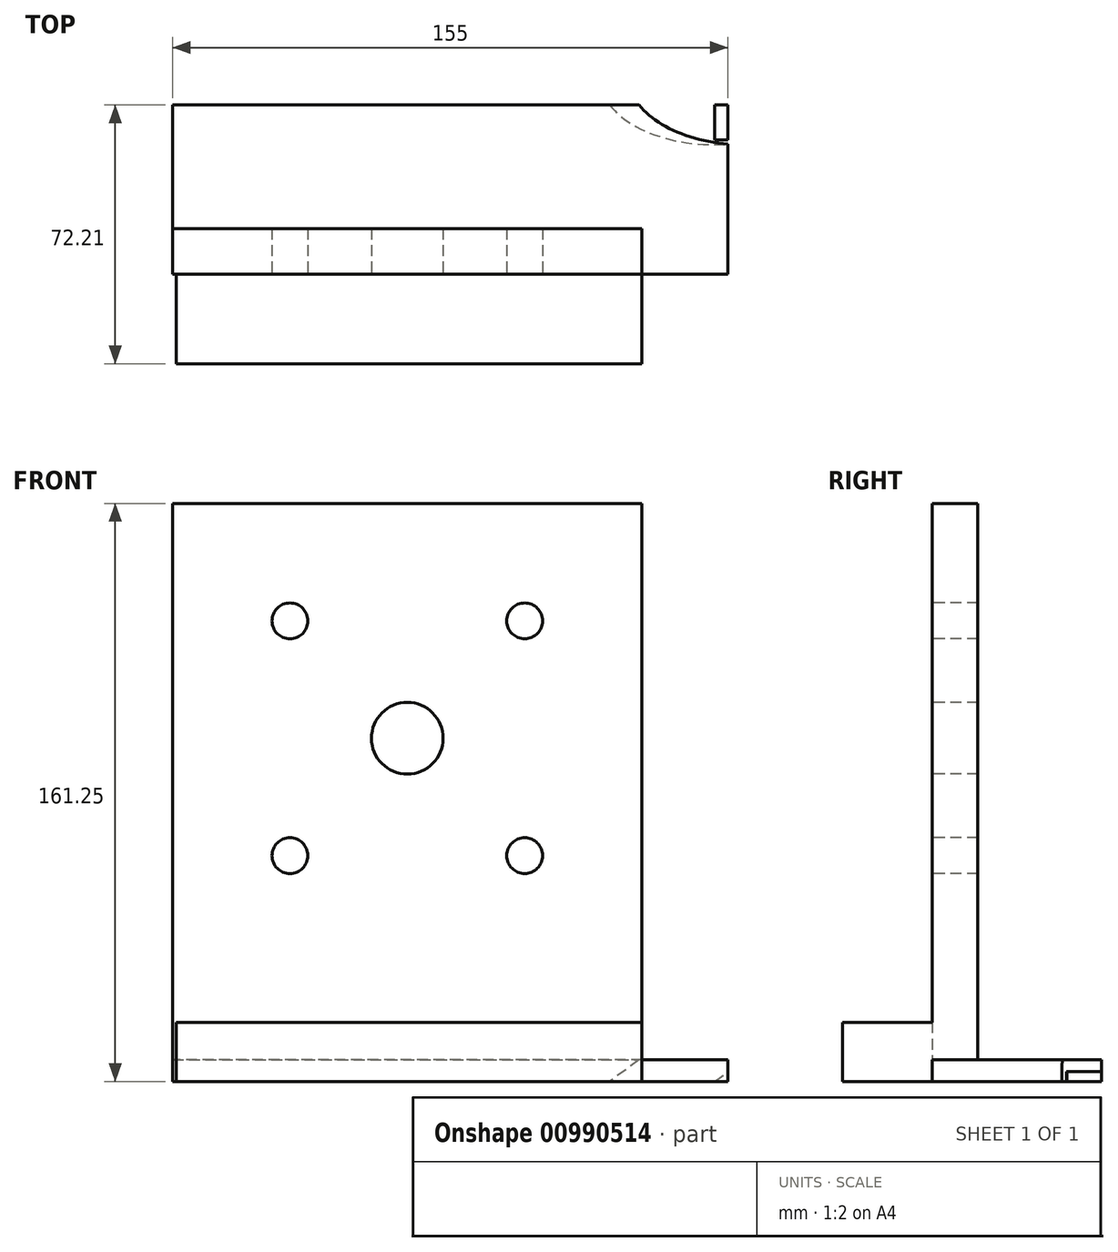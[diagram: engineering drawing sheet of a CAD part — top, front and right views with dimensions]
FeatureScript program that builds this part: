
annotation { "Feature Type Name" : "Feature", "Feature Type Description" : "" }
export const myFeature = defineFeature(function(context is Context, id is Id, definition is map)
    precondition{}
    {
        {
            var Q0;
            Q0=qCreatedBy(makeId("Front.planeOp"),FACE);
            var sketch = newSketch(context, id + "F0", { "sketchPlane" : qUnion([Q0])});
            skLineSegment(sketch, "E0.bottom", {"start": v(65.5, 0) * mm, "end": v(-65.5, 0) * mm});
            skLineSegment(sketch, "E0.top", {"start": v(65.5, 155.25) * mm, "end": v(-65.5, 155.25) * mm});
            skLineSegment(sketch, "E0.left", {"start": v(65.5, 0) * mm, "end": v(65.5, 155.25) * mm});
            skLineSegment(sketch, "E0.right", {"start": v(-65.5, 0) * mm, "end": v(-65.5, 155.25) * mm});
            skLineSegment(sketch, "E1.bottom", {"start": v(-65.5, 0) * mm, "end": v(89.5, 0) * mm});
            skLineSegment(sketch, "E1.top", {"start": v(-65.5, -12.7) * mm, "end": v(89.5, -12.7) * mm});
            skLineSegment(sketch, "E1.left", {"start": v(-65.5, 0) * mm, "end": v(-65.5, -12.7) * mm});
            skLineSegment(sketch, "E1.right", {"start": v(89.5, 0) * mm, "end": v(89.5, -12.7) * mm});
            skCircle(sketch, "E2", {"center": v(-32.75, 57) * mm, "radius": 5 * mm});
            skCircle(sketch, "E3.0.1.0", {"center": v(-32.75, 122.5) * mm, "radius": 5 * mm});
            skCircle(sketch, "E3.1.0.0", {"center": v(32.75, 57) * mm, "radius": 5 * mm});
            skCircle(sketch, "E3.1.1.0", {"center": v(32.75, 122.5) * mm, "radius": 5 * mm});
            skLineSegment(sketch, "E3.direction1", {"start": v(-32.75, 57) * mm, "end": v(32.75, 57) * mm, "construction": true});
            skLineSegment(sketch, "E3.direction2", {"start": v(-32.75, 57) * mm, "end": v(-32.75, 122.5) * mm, "construction": true});
            skCircle(sketch, "E4", {"center": v(0, 89.75) * mm, "radius": 10 * mm});
            skSolve(sketch);
        }
        {
            var Q0;
            Q0=makeQuery(id+"F0.imprint","IMPRINT",FACE,{"disambiguationData":[TD([[makeQuery(id+"F0.imprint","IMPRINT",EDGE,{"derivedFrom":sQuery(id+"F0.wireOp",EDGE,"E0.top")}),1.0]])]});
            extrude(context, id + "F1", {"entities" : qUnion([Q0]), "oppositeDirection" : true, "depth" : 12.7 * mm, "offsetDistance" : 25 * mm});
        }
        {
            var Q0;
            Q0=makeQuery(id+"F0.imprint","IMPRINT",FACE,{"disambiguationData":[TD([[makeQuery(id+"F0.imprint","IMPRINT",EDGE,{"derivedFrom":sQuery(id+"F0.wireOp",EDGE,"E1.bottom")}),-1.0]])]});
            extrude(context, id + "F2", {"entities" : qUnion([Q0]), "operationType" : NewBodyOperationType.ADD, "oppositeDirection" : true, "depth" : 150 * mm, "offsetDistance" : 25 * mm});
        }
        {
            var Q0;
            Q0=makeQuery(id+"F2.opExtrude","SWEPT_FACE",FACE,{"disambiguationData":[OSD([sQuery(id+"F0.wireOp",EDGE,"E1.top")])]});
            var sketch = newSketch(context, id + "F3", { "sketchPlane" : qUnion([Q0])});
            skLineSegment(sketch, "E5", {"start": v(89.5, -12.7) * mm, "end": v(-65.5, -12.7) * mm});
            skCircle(sketch, "E6", {"center": v(-40, -55.7) * mm, "radius": 4.76 * mm});
            skCircle(sketch, "E7.0.1.0", {"center": v(-40, -118.2) * mm, "radius": 4.76 * mm});
            skCircle(sketch, "E7.1.0.0", {"center": v(64, -55.7) * mm, "radius": 4.76 * mm});
            skCircle(sketch, "E7.1.1.0", {"center": v(64, -118.2) * mm, "radius": 4.76 * mm});
            skLineSegment(sketch, "E7.direction1", {"start": v(-40, -55.7) * mm, "end": v(64, -55.7) * mm, "construction": true});
            skLineSegment(sketch, "E7.direction2", {"start": v(-40, -55.7) * mm, "end": v(-40, -118.2) * mm, "construction": true});
            skSolve(sketch);
        }
        {
            var Q0;
            Q0=makeQuery(id+"F3.imprint","IMPRINT",FACE,{"disambiguationData":[TD([[makeQuery(id+"F3.imprint","IMPRINT",EDGE,{"derivedFrom":sQuery(id+"F3.wireOp",EDGE,"E6")}),1.0]])]});
            var Q1;
            Q1=makeQuery(id+"F3.imprint","IMPRINT",FACE,{"disambiguationData":[TD([[makeQuery(id+"F3.imprint","IMPRINT",EDGE,{"derivedFrom":sQuery(id+"F3.wireOp",EDGE,"E7.0.1.0")}),1.0]])]});
            var Q2;
            Q2=makeQuery(id+"F3.imprint","IMPRINT",FACE,{"disambiguationData":[TD([[makeQuery(id+"F3.imprint","IMPRINT",EDGE,{"derivedFrom":sQuery(id+"F3.wireOp",EDGE,"E7.1.1.0")}),1.0]])]});
            var Q3;
            Q3=makeQuery(id+"F3.imprint","IMPRINT",FACE,{"disambiguationData":[TD([[makeQuery(id+"F3.imprint","IMPRINT",EDGE,{"derivedFrom":sQuery(id+"F3.wireOp",EDGE,"E7.1.0.0")}),1.0]])]});
            extrude(context, id + "F4", {"entities" : qUnion([Q0, Q1, Q2, Q3]), "operationType" : NewBodyOperationType.REMOVE, "endBound" : BoundingType.THROUGH_ALL, "oppositeDirection" : true, "depth" : 25 * mm, "offsetDistance" : 25 * mm});
        }
        {
            var Q0;
            {var subQ0=sQuery(id+"F0.wireOp",EDGE,"E1.bottom");Q0=makeQuery(id+"F2.boolean.opBoolean","MERGE",FACE,{"derivedFrom":[makeQuery(id+"F1.opExtrude","CAP_FACE",FACE,{"disambiguationData":[OSD([sQuery(id+"F0.wireOp",EDGE,"E0.top"),sQuery(id+"F0.wireOp",EDGE,"E0.left"),sQuery(id+"F0.wireOp",EDGE,"E0.right"),subQ0,sQuery(id+"F0.wireOp",EDGE,"E2"),sQuery(id+"F0.wireOp",EDGE,"E3.0.1.0"),sQuery(id+"F0.wireOp",EDGE,"E3.1.0.0"),sQuery(id+"F0.wireOp",EDGE,"E3.1.1.0"),sQuery(id+"F0.wireOp",EDGE,"E4")])],"isStart":true}),makeQuery(id+"F2.opExtrude","CAP_FACE",FACE,{"disambiguationData":[OSD([subQ0,sQuery(id+"F0.wireOp",EDGE,"E1.top"),sQuery(id+"F0.wireOp",EDGE,"E1.left"),sQuery(id+"F0.wireOp",EDGE,"E1.right")])],"isStart":true})]});}
            var sketch = newSketch(context, id + "F5", { "sketchPlane" : qUnion([Q0])});
            skLineSegment(sketch, "E8", {"start": v(-63.5, -12.7) * mm, "end": v(-44.93, -100.76) * mm});
            skLineSegment(sketch, "E9", {"start": v(-44.93, -100.76) * mm, "end": v(76.5, -12.7) * mm});
            skSolve(sketch);
        }
        {
            var Q0;
            {var subQ0=sQuery(id+"F5.wireOp",EDGE,"E8");Q0=makeQuery(id+"F5.imprint","IMPRINT",FACE,{"disambiguationData":[TD([[makeQuery(id+"F5.imprint","IMPRINT",EDGE,{"derivedFrom":subQ0}),1.0]])]});}
            extrude(context, id + "F6", {"entities" : qUnion([Q0]), "operationType" : NewBodyOperationType.ADD, "oppositeDirection" : true, "depth" : 55 * mm, "offsetDistance" : 25 * mm});
        }
        {
            var Q0;
            Q0=makeQuery(id+"F6.opExtrude","SWEPT_FACE",FACE,{"disambiguationData":[OSD([sQuery(id+"F5.wireOp",EDGE,"E9")])]});
            var sketch = newSketch(context, id + "F7", { "sketchPlane" : qUnion([Q0])});
            skLineSegment(sketch, "E10", {"start": v(54.47, -55) * mm, "end": v(-45.53, -55) * mm});
            skLineSegment(sketch, "E11", {"start": v(-45.53, -55) * mm, "end": v(-45.53, -30) * mm});
            skLineSegment(sketch, "E12", {"start": v(-45.53, -30) * mm, "end": v(54.47, -30) * mm});
            skLineSegment(sketch, "E13", {"start": v(54.47, -30) * mm, "end": v(54.47, -55) * mm});
            skLineSegment(sketch, "E14", {"start": v(-45.53, -37.5) * mm, "end": v(18.27, -37.5) * mm});
            skLineSegment(sketch, "E15", {"start": v(18.27, -37.5) * mm, "end": v(54.47, -37.5) * mm});
            skSolve(sketch);
        }
        {
            var Q0;
            {var subQ2=sQuery(id+"F7.wireOp",EDGE,"E12");Q0=makeQuery(id+"F7.imprint","IMPRINT",FACE,{"disambiguationData":[TD([[makeQuery(id+"F7.imprint","IMPRINT",EDGE,{"derivedFrom":subQ2}),-1.0]])]});}
            var Q1;
            Q1=sQuery(id+"F7.wireOp",EDGE,"E10");
            revolve(context, id + "F8", {"operationType" : NewBodyOperationType.ADD, "surfaceOperationType" : NewSurfaceOperationType.NEW, "entities" : qUnion([Q0]), "axis" : qUnion([Q1]), "revolveType" : RevolveType.FULL, "oppositeDirection" : true});
        }
        {
            var Q0;
            Q0=makeQuery(id+"F2.opExtrude","SWEPT_FACE",FACE,{"disambiguationData":[OSD([sQuery(id+"F0.wireOp",EDGE,"E1.right")])]});
            var sketch = newSketch(context, id + "F9", { "sketchPlane" : qUnion([Q0])});
            skLineSegment(sketch, "E16.bottom", {"start": v(34.14, 0) * mm, "end": v(80.6, 0) * mm});
            skLineSegment(sketch, "E16.top", {"start": v(34.14, 23.6) * mm, "end": v(80.6, 23.6) * mm});
            skLineSegment(sketch, "E16.left", {"start": v(34.14, 0) * mm, "end": v(34.14, 23.6) * mm});
            skLineSegment(sketch, "E16.right", {"start": v(80.6, 0) * mm, "end": v(80.6, 23.6) * mm});
            skSolve(sketch);
        }
        {
            var Q0;
            Q0=makeQuery(id+"F9.imprint","IMPRINT",FACE,{"disambiguationData":[TD([[makeQuery(id+"F9.imprint","IMPRINT",EDGE,{"derivedFrom":sQuery(id+"F9.wireOp",EDGE,"E16.bottom")}),-1.0]])]});
            extrude(context, id + "F10", {"entities" : qUnion([Q0]), "operationType" : NewBodyOperationType.REMOVE, "oppositeDirection" : true, "depth" : 100.62 * mm, "offsetDistance" : 25 * mm});
        }
        {
            var Q0;
            Q0=qCreatedBy(makeId("Front.planeOp"),FACE);
            var sketch = newSketch(context, id + "F11", { "sketchPlane" : qUnion([Q0])});
            skLineSegment(sketch, "E17.bottom", {"start": v(-4.59, -72.84) * mm, "end": v(-55.62, -72.84) * mm});
            skLineSegment(sketch, "E17.top", {"start": v(-4.59, -104.11) * mm, "end": v(-55.62, -104.11) * mm});
            skLineSegment(sketch, "E17.left", {"start": v(-4.59, -72.84) * mm, "end": v(-4.59, -104.11) * mm});
            skLineSegment(sketch, "E17.right", {"start": v(-55.62, -72.84) * mm, "end": v(-55.62, -104.11) * mm});
            skLineSegment(sketch, "E18.bottom", {"start": v(-63.9, -12.7) * mm, "end": v(-44.63, -12.7) * mm});
            skLineSegment(sketch, "E18.top", {"start": v(-63.9, -72.84) * mm, "end": v(-44.63, -72.84) * mm});
            skLineSegment(sketch, "E18.left", {"start": v(-63.9, -12.7) * mm, "end": v(-63.9, -72.84) * mm});
            skLineSegment(sketch, "E18.right", {"start": v(-44.63, -12.7) * mm, "end": v(-44.63, -72.84) * mm});
            skSolve(sketch);
        }
        {
            var Q0;
            Q0=makeQuery(id+"F11.imprint","IMPRINT",FACE,{"disambiguationData":[TD([[makeQuery(id+"F11.imprint","IMPRINT",EDGE,{"derivedFrom":sQuery(id+"F11.wireOp",EDGE,"E18.bottom")}),-1.0]])]});
            var Q1;
            {var subQ1=sQuery(id+"F11.wireOp",EDGE,"E17.bottom");Q1=makeQuery(id+"F11.imprint","IMPRINT",FACE,{"disambiguationData":[TD([[makeQuery(id+"F11.imprint","IMPRINT",EDGE,{"derivedFrom":subQ1}),1.0]])]});}
            extrude(context, id + "F12", {"entities" : qUnion([Q0, Q1]), "operationType" : NewBodyOperationType.REMOVE, "endBound" : BoundingType.THROUGH_ALL, "oppositeDirection" : true, "depth" : 63.06 * mm, "offsetDistance" : 25 * mm});
        }
        {
            var Q0;
            Q0=makeQuery(id+"F6.opExtrude","CAP_FACE",FACE,{"disambiguationData":[OSD([sQuery(id+"F0.wireOp",EDGE,"E1.top"),sQuery(id+"F5.wireOp",EDGE,"E8"),sQuery(id+"F5.wireOp",EDGE,"E9")])],"isStart":false});
            var sketch = newSketch(context, id + "F13", { "sketchPlane" : qUnion([Q0])});
            skLineSegment(sketch, "E19", {"start": v(19.13, -51.17) * mm, "end": v(-10.05, -91.4) * mm});
            skLineSegment(sketch, "E20", {"start": v(-10.05, -91.4) * mm, "end": v(37.2, -125.68) * mm});
            skLineSegment(sketch, "E21", {"start": v(37.2, -125.68) * mm, "end": v(76.4, -71.65) * mm});
            skLineSegment(sketch, "E22", {"start": v(76.4, -71.65) * mm, "end": v(19.13, -51.17) * mm});
            skSolve(sketch);
        }
        {
            var Q0;
            {var subQ10=sQuery(id+"F13.wireOp",EDGE,"E20");Q0=makeQuery(id+"F13.imprint","IMPRINT",FACE,{"disambiguationData":[TD([[makeQuery(id+"F13.imprint","IMPRINT",EDGE,{"derivedFrom":subQ10}),1.0]])]});}
            var Q1;
            {var subQ0=sQuery(id+"F5.wireOp",EDGE,"E9");var subQ1=makeQuery(id+"F6.opExtrude","CAP_FACE",FACE,{"disambiguationData":[OSD([sQuery(id+"F0.wireOp",EDGE,"E1.top"),sQuery(id+"F5.wireOp",EDGE,"E8"),subQ0])],"isStart":false});var subQ2=subQ1;var subQ3=makeQuery(id+"F12.boolean.opBoolean","INTERSECT",EDGE,{"derivedFrom":[subQ2,makeQuery(id+"F12.opExtrude","SWEPT_FACE",FACE,{"disambiguationData":[OSD([sQuery(id+"F11.wireOp",EDGE,"E17.bottom")])]})]});Q1=makeQuery(id+"F13.imprint","IMPRINT",FACE,{"disambiguationData":[TD([[makeQuery(id+"F13.imprint","IMPRINT",EDGE,{"derivedFrom":subQ3}),1.0]])]});}
            extrude(context, id + "F14", {"entities" : qUnion([Q0, Q1]), "operationType" : NewBodyOperationType.REMOVE, "oppositeDirection" : true, "depth" : 89 * mm, "offsetDistance" : 25 * mm});
        }
        {
            var Q0;
            Q0=makeQuery(id+"F14.boolean.opBoolean","MERGE",FACE,{"derivedFrom":[makeQuery(id+"F8.opRevolve","SWEPT_FACE",FACE,{"disambiguationData":[OSD([sQuery(id+"F7.wireOp",EDGE,"E11")])]})],"fromTools":[makeQuery(id+"F14.opExtrude","SWEPT_FACE",FACE,{"disambiguationData":[OSD([sQuery(id+"F13.wireOp",EDGE,"E19")])]})]});
            var sketch = newSketch(context, id + "F15", { "sketchPlane" : qUnion([Q0])});
            skCircle(sketch, "E23", {"center": v(-55, -55.2) * mm, "radius": 18.87 * mm});
            skSolve(sketch);
        }
        {
            var Q0;
            {var subQ0=sQuery(id+"F13.wireOp",EDGE,"E19");Q0=makeQuery(id+"F15.imprint","IMPRINT",FACE,{"disambiguationData":[TD([[makeQuery(id+"F15.imprint","IMPRINT",EDGE,{"derivedFrom":makeQuery(id+"F14.boolean.opBoolean","COPY",EDGE,{"derivedFrom":makeQuery(id+"F14.opExtrude","CAP_EDGE",EDGE,{"disambiguationData":[OSD([subQ0])],"isStart":true})})}),-1.0]])]});}
            var Q1;
            Q1=makeQuery(id+"F15.imprint","IMPRINT",FACE,{"disambiguationData":[TD([[makeQuery(id+"F15.imprint","IMPRINT",EDGE,{"derivedFrom":sQuery(id+"F15.wireOp",EDGE,"E23")}),1.0]])]});
            extrude(context, id + "F16", {"entities" : qUnion([Q0, Q1]), "operationType" : NewBodyOperationType.REMOVE, "endBound" : BoundingType.THROUGH_ALL, "oppositeDirection" : true, "depth" : 25 * mm, "offsetDistance" : 25 * mm});
        }
        {
            var Q0;
            {var subQ1=sQuery(id+"F0.wireOp",EDGE,"E1.right");var subQ3=sQuery(id+"F0.wireOp",EDGE,"E1.top");var subQ6=makeQuery(id+"F2.opExtrude","SWEPT_FACE",FACE,{"disambiguationData":[OSD([subQ3])]});var subQ14=makeQuery(id+"F2.opExtrude","SWEPT_FACE",FACE,{"disambiguationData":[OSD([subQ1])]});var subQ17=makeQuery(id+"F4.boolean.opBoolean","COPY",FACE,{"derivedFrom":makeQuery(id+"F4.opExtrude","SWEPT_FACE",FACE,{"disambiguationData":[OSD([sQuery(id+"F3.wireOp",EDGE,"E6")])]})});Q0=makeQuery(id+"F16.boolean.opBoolean","SPLIT",FACE,{"disambiguationData":[TD([subQ17])],"derivedFrom":makeQuery(id+"F12.boolean.opBoolean","SPLIT",FACE,{"disambiguationData":[TD([subQ14])],"derivedFrom":subQ6})});}
            cPlane(context, id + "F17", {"entities" : qUnion([Q0]), "cplaneType" : CPlaneType.OFFSET, "offset" : 57.01 * mm, "width" : 150 * mm, "height" : 150 * mm});
        }
        {
            var Q0;
            Q0=qCreatedBy(id+"F17.planeOp",FACE);
            var sketch = newSketch(context, id + "F18", { "sketchPlane" : qUnion([Q0])});
            skLineSegment(sketch, "E24.bottom", {"start": v(-26.24, -39.17) * mm, "end": v(-54.25, -39.17) * mm});
            skLineSegment(sketch, "E24.top", {"start": v(-26.24, -72.55) * mm, "end": v(-54.25, -72.55) * mm});
            skLineSegment(sketch, "E24.left", {"start": v(-26.24, -39.17) * mm, "end": v(-26.24, -72.55) * mm});
            skLineSegment(sketch, "E24.right", {"start": v(-54.25, -39.17) * mm, "end": v(-54.25, -72.55) * mm});
            skSolve(sketch);
        }
        {
            var Q0;
            Q0=makeQuery(id+"F18.imprint","IMPRINT",FACE,{"disambiguationData":[TD([[makeQuery(id+"F18.imprint","IMPRINT",EDGE,{"derivedFrom":sQuery(id+"F18.wireOp",EDGE,"E24.bottom")}),1.0]])]});
            extrude(context, id + "F19", {"entities" : qUnion([Q0]), "operationType" : NewBodyOperationType.REMOVE, "oppositeDirection" : true, "depth" : 57.44 * mm, "offsetDistance" : 25 * mm});
        }
        {
            var Q0;
            {var subQ1=sQuery(id+"F0.wireOp",EDGE,"E1.right");var subQ3=sQuery(id+"F0.wireOp",EDGE,"E1.top");var subQ6=makeQuery(id+"F2.opExtrude","SWEPT_FACE",FACE,{"disambiguationData":[OSD([subQ3])]});var subQ14=makeQuery(id+"F2.opExtrude","SWEPT_FACE",FACE,{"disambiguationData":[OSD([subQ1])]});var subQ17=makeQuery(id+"F4.boolean.opBoolean","COPY",FACE,{"derivedFrom":makeQuery(id+"F4.opExtrude","SWEPT_FACE",FACE,{"disambiguationData":[OSD([sQuery(id+"F3.wireOp",EDGE,"E6")])]})});Q0=makeQuery(id+"F16.boolean.opBoolean","SPLIT",FACE,{"disambiguationData":[TD([subQ17])],"derivedFrom":makeQuery(id+"F12.boolean.opBoolean","SPLIT",FACE,{"disambiguationData":[TD([subQ14])],"derivedFrom":subQ6})});}
            cPlane(context, id + "F20", {"entities" : qUnion([Q0]), "cplaneType" : CPlaneType.OFFSET, "offset" : 94.9 * mm, "width" : 150 * mm, "height" : 150 * mm});
        }
        {
            var Q0;
            Q0=makeQuery(id+"F2.opExtrude","CAP_FACE",FACE,{"disambiguationData":[OSD([sQuery(id+"F0.wireOp",EDGE,"E1.bottom"),sQuery(id+"F0.wireOp",EDGE,"E1.top"),sQuery(id+"F0.wireOp",EDGE,"E1.left"),sQuery(id+"F0.wireOp",EDGE,"E1.right")])],"isStart":false});
            cPlane(context, id + "F21", {"entities" : qUnion([Q0]), "cplaneType" : CPlaneType.OFFSET, "offset" : 83.64 * mm, "oppositeDirection" : true, "width" : 150 * mm, "height" : 150 * mm});
        }
        {
            var Q0;
            Q0=qCreatedBy(id+"F21.planeOp",FACE);
            var sketch = newSketch(context, id + "F22", { "sketchPlane" : qUnion([Q0])});
            skLineSegment(sketch, "E25.bottom", {"start": v(-19.5, -47.14) * mm, "end": v(25.5, -47.14) * mm});
            skLineSegment(sketch, "E25.top", {"start": v(-19.5, -10.84) * mm, "end": v(25.5, -10.84) * mm});
            skLineSegment(sketch, "E25.left", {"start": v(-19.5, -47.14) * mm, "end": v(-19.5, -10.84) * mm});
            skLineSegment(sketch, "E25.right", {"start": v(25.5, -47.14) * mm, "end": v(25.5, -10.84) * mm});
            skLineSegment(sketch, "E26", {"start": v(9.29, -47.14) * mm, "end": v(-19.5, -25.37) * mm});
            skSolve(sketch);
        }
        {
            var Q0;
            {var subQ2=sQuery(id+"F22.wireOp",EDGE,"E25.top");Q0=makeQuery(id+"F22.imprint","IMPRINT",FACE,{"disambiguationData":[TD([[makeQuery(id+"F22.imprint","IMPRINT",EDGE,{"derivedFrom":subQ2}),-1.0]])]});}
            extrude(context, id + "F23", {"entities" : qUnion([Q0]), "operationType" : NewBodyOperationType.ADD, "oppositeDirection" : true, "depth" : 37.3 * mm, "offsetDistance" : 25 * mm});
        }
        {
            var Q0;
            Q0=qCreatedBy(id+"F20.planeOp",FACE);
            var sketch = newSketch(context, id + "F24", { "sketchPlane" : qUnion([Q0])});
            skLineSegment(sketch, "E27", {"start": v(-70.25, -47.2) * mm, "end": v(105.05, -47.2) * mm});
            skLineSegment(sketch, "E28", {"start": v(105.05, -47.2) * mm, "end": v(105.05, 16.74) * mm});
            skLineSegment(sketch, "E29", {"start": v(105.05, 16.74) * mm, "end": v(-70.14, 16.74) * mm});
            skLineSegment(sketch, "E30", {"start": v(-70.14, 16.74) * mm, "end": v(-70.25, -47.2) * mm});
            skLineSegment(sketch, "E31", {"start": v(-70.25, -47.2) * mm, "end": v(-70.25, -164.49) * mm});
            skLineSegment(sketch, "E32", {"start": v(-70.25, -164.49) * mm, "end": v(108.53, -164.49) * mm});
            skLineSegment(sketch, "E33", {"start": v(108.53, -164.49) * mm, "end": v(105.05, -47.2) * mm});
            skSolve(sketch);
        }
        {
            var Q0;
            Q0=makeQuery(id+"F24.imprint","IMPRINT",FACE,{"disambiguationData":[TD([[makeQuery(id+"F24.imprint","IMPRINT",EDGE,{"derivedFrom":sQuery(id+"F24.wireOp",EDGE,"E27")}),-1.0]])]});
            extrude(context, id + "F25", {"entities" : qUnion([Q0]), "operationType" : NewBodyOperationType.REMOVE, "endBound" : BoundingType.THROUGH_ALL, "oppositeDirection" : true, "depth" : 25 * mm, "offsetDistance" : 25 * mm});
        }
        {
            var Q0;
            Q0=qCreatedBy(makeId("Front.planeOp"),FACE);
            var sketch = newSketch(context, id + "F26", { "sketchPlane" : qUnion([Q0])});
            skLineSegment(sketch, "E34.bottom", {"start": v(65.5, 10.5) * mm, "end": v(-64.5, 10.5) * mm});
            skLineSegment(sketch, "E34.top", {"start": v(65.5, -22.5) * mm, "end": v(-64.5, -22.5) * mm});
            skLineSegment(sketch, "E34.left", {"start": v(65.5, 10.5) * mm, "end": v(65.5, -22.5) * mm});
            skLineSegment(sketch, "E34.right", {"start": v(-64.5, 10.5) * mm, "end": v(-64.5, -22.5) * mm});
            skSolve(sketch);
        }
        {
            var Q0;
            Q0=makeQuery(id+"F26.imprint","IMPRINT",FACE,{"disambiguationData":[TD([[makeQuery(id+"F26.imprint","IMPRINT",EDGE,{"derivedFrom":sQuery(id+"F26.wireOp",EDGE,"E34.bottom")}),1.0]])]});
            extrude(context, id + "F27", {"entities" : qUnion([Q0]), "operationType" : NewBodyOperationType.ADD, "depth" : 25 * mm, "offsetDistance" : 25 * mm});
        }
        {
            var Q0;
            {var subQ2=sQuery(id+"F0.wireOp",EDGE,"E1.top");var subQ8=sQuery(id+"F26.wireOp",EDGE,"E34.top");var subQ9=sQuery(id+"F26.wireOp",EDGE,"E34.right");Q0=makeQuery(id+"F27.boolean.opBoolean","SPLIT",FACE,{"disambiguationData":[TD([makeQuery(id+"F2.opExtrude","SWEPT_FACE",FACE,{"disambiguationData":[OSD([subQ2])]})])],"derivedFrom":makeQuery(id+"F27.opExtrude","CAP_FACE",FACE,{"disambiguationData":[OSD([sQuery(id+"F26.wireOp",EDGE,"E34.bottom"),subQ8,sQuery(id+"F26.wireOp",EDGE,"E34.left"),subQ9])],"isStart":true})});}
            extrude(context, id + "F28", {"entities" : qUnion([Q0]), "operationType" : NewBodyOperationType.ADD, "depth" : 47.17 * mm, "offsetDistance" : 25 * mm});
        }
        {
            var Q0;
            Q0=makeQuery(id+"F27.opExtrude","CAP_FACE",FACE,{"disambiguationData":[OSD([sQuery(id+"F26.wireOp",EDGE,"E34.bottom"),sQuery(id+"F26.wireOp",EDGE,"E34.top"),sQuery(id+"F26.wireOp",EDGE,"E34.left"),sQuery(id+"F26.wireOp",EDGE,"E34.right")])],"isStart":false});
            var sketch = newSketch(context, id + "F29", { "sketchPlane" : qUnion([Q0])});
            skLineSegment(sketch, "E35", {"start": v(102.44, -6) * mm, "end": v(-95.08, -6) * mm});
            skLineSegment(sketch, "E36", {"start": v(102.44, -6) * mm, "end": v(102.44, -90.83) * mm});
            skLineSegment(sketch, "E37", {"start": v(102.44, -90.83) * mm, "end": v(-96.5, -90.83) * mm});
            skLineSegment(sketch, "E38", {"start": v(-96.5, -90.83) * mm, "end": v(-95.08, -6) * mm});
            skLineSegment(sketch, "E39", {"start": v(-95.08, -6) * mm, "end": v(-95.08, 171.2) * mm});
            skLineSegment(sketch, "E40", {"start": v(-95.08, 171.2) * mm, "end": v(114.36, 171.2) * mm});
            skLineSegment(sketch, "E41", {"start": v(114.36, 171.2) * mm, "end": v(102.44, -6) * mm});
            skSolve(sketch);
        }
        {
            var Q0;
            {var subQ0=sQuery(id+"F29.wireOp",EDGE,"E36");Q0=makeQuery(id+"F29.imprint","IMPRINT",FACE,{"disambiguationData":[TD([[makeQuery(id+"F29.imprint","IMPRINT",EDGE,{"derivedFrom":subQ0}),-1.0]])]});}
            var Q1;
            {var subQ5=makeQuery(id+"F27.opExtrude","CAP_EDGE",EDGE,{"disambiguationData":[OSD([sQuery(id+"F26.wireOp",EDGE,"E34.top")])],"isStart":false});Q1=makeQuery(id+"F29.imprint","IMPRINT",FACE,{"disambiguationData":[TD([[makeQuery(id+"F29.imprint","IMPRINT",EDGE,{"derivedFrom":subQ5}),-1.0]])]});}
            extrude(context, id + "F30", {"entities" : qUnion([Q0, Q1]), "operationType" : NewBodyOperationType.REMOVE, "oppositeDirection" : true, "depth" : 374 * mm, "offsetDistance" : 25 * mm});
        }
    });
